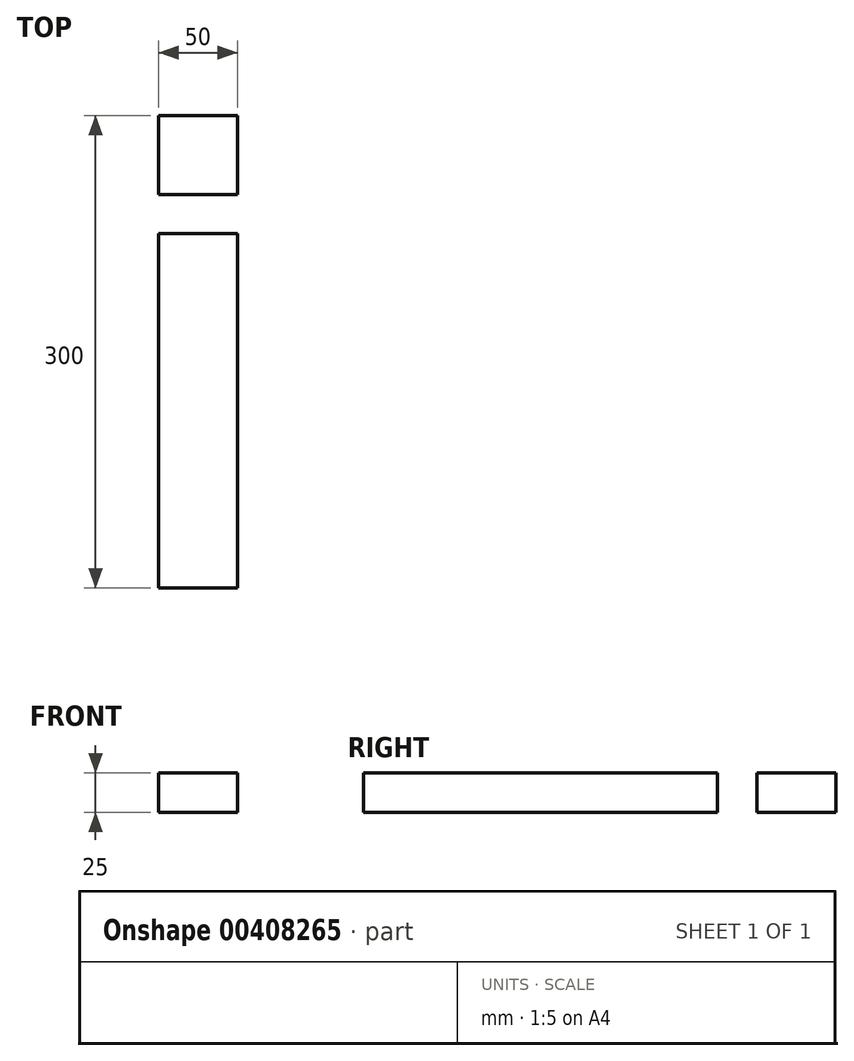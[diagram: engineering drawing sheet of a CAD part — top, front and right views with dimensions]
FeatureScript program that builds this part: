
annotation { "Feature Type Name" : "Feature", "Feature Type Description" : "" }
export const myFeature = defineFeature(function(context is Context, id is Id, definition is map)
    precondition{}
    {
        {
            var Q0;
            Q0=qCreatedBy(makeId("Top.planeOp"),FACE);
            var sketch = newSketch(context, id + "F0", { "sketchPlane" : qUnion([Q0])});
            skLineSegment(sketch, "E0.bottom", {"start": v(25, -112.5) * mm, "end": v(-25, -112.5) * mm});
            skLineSegment(sketch, "E0.top", {"start": v(25, 112.5) * mm, "end": v(-25, 112.5) * mm});
            skLineSegment(sketch, "E0.left", {"start": v(25, -112.5) * mm, "end": v(25, 112.5) * mm});
            skLineSegment(sketch, "E0.right", {"start": v(-25, -112.5) * mm, "end": v(-25, 112.5) * mm});
            skPoint(sketch, "E0.middle", {"position": v(0, 0) * mm});
            skLineSegment(sketch, "E1.bottom", {"start": v(25, 137.5) * mm, "end": v(-25, 137.5) * mm});
            skLineSegment(sketch, "E1.top", {"start": v(25, 187.5) * mm, "end": v(-25, 187.5) * mm});
            skLineSegment(sketch, "E1.left", {"start": v(25, 137.5) * mm, "end": v(25, 187.5) * mm});
            skLineSegment(sketch, "E1.right", {"start": v(-25, 137.5) * mm, "end": v(-25, 187.5) * mm});
            skPoint(sketch, "E1.middle", {"position": v(0, 162.5) * mm});
            skSolve(sketch);
        }
        {
            var Q0;
            Q0 = qSketchRegion(id + "F0", true);
            extrude(context, id + "F1", {"entities" : qUnion([Q0]), "depth" : 25 * mm});
        }
    });
